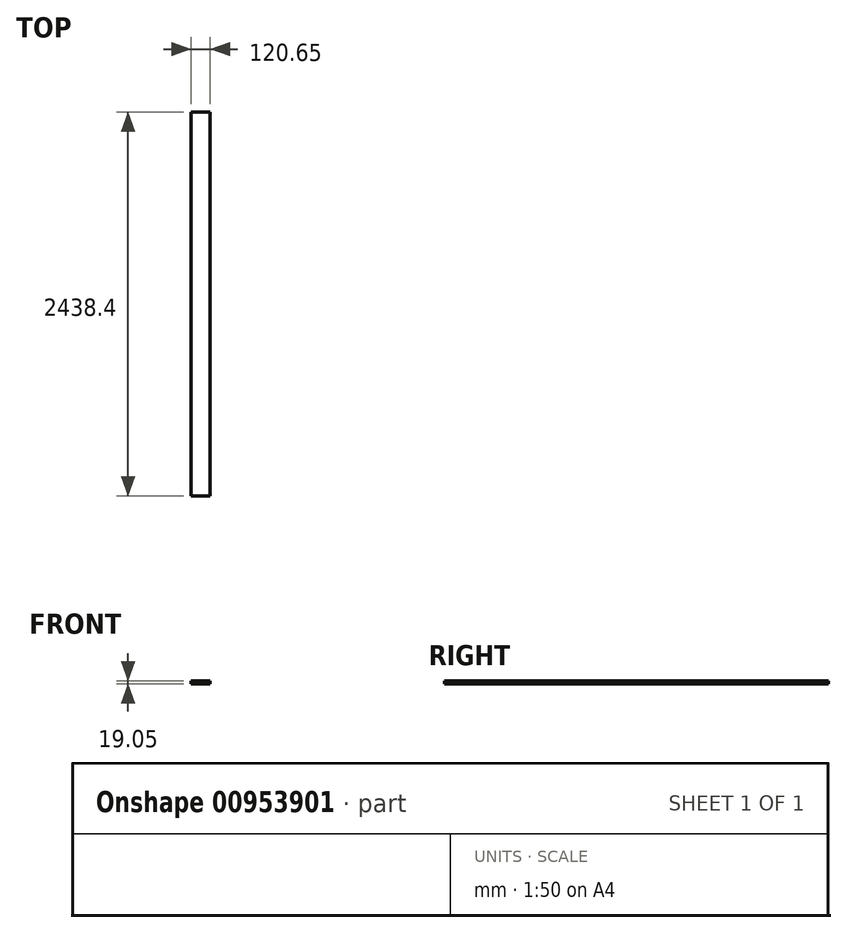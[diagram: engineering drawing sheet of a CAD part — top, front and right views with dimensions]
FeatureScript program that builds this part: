
annotation { "Feature Type Name" : "Feature", "Feature Type Description" : "" }
export const myFeature = defineFeature(function(context is Context, id is Id, definition is map)
    precondition{}
    {
        {
            var Q0;
            Q0=qCreatedBy(makeId("Top.planeOp"),FACE);
            var sketch = newSketch(context, id + "F0", { "sketchPlane" : qUnion([Q0])});
            skLineSegment(sketch, "E0.bottom", {"start": v(0, 0) * mm, "end": v(120.65, 0) * mm});
            skLineSegment(sketch, "E0.top", {"start": v(0, 2438.4) * mm, "end": v(120.65, 2438.4) * mm});
            skLineSegment(sketch, "E0.left", {"start": v(0, 0) * mm, "end": v(0, 2438.4) * mm});
            skLineSegment(sketch, "E0.right", {"start": v(120.65, 0) * mm, "end": v(120.65, 2438.4) * mm});
            skSolve(sketch);
        }
        {
            var Q0;
            Q0 = qSketchRegion(id + "F0", true);
            extrude(context, id + "F1", {"entities" : qUnion([Q0]), "depth" : 19.05 * mm, "offsetDistance" : 25.4 * mm});
        }
    });
